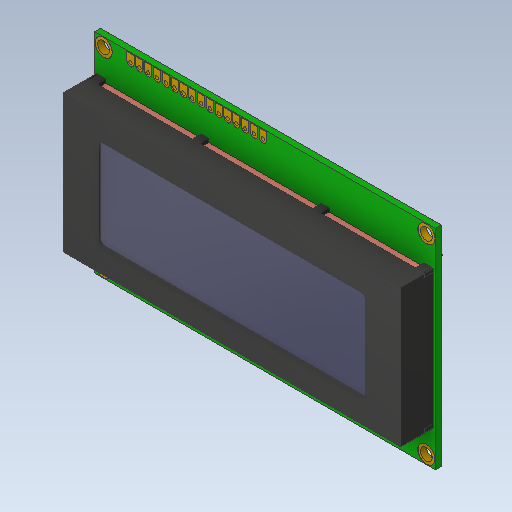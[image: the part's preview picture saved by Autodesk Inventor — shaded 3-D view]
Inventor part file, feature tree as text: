
AUTODESK INVENTOR PART (.ipt)
format: ipt  version: 2020 (Build 240168000, 168)  size: 613,888 bytes
history: native  units: in
note: dims shown in document units (in); Inventor stores cm internally (conversion verified against a paired STEP export)
features: sketch x10, extrude x8, projected_geometry x6, mirror x3, hole x2, fillet x2
ambient origin geometry x8: Origin, YZ Plane, XZ Plane, XY Plane, X Axis, Y Axis, Z Axis, Center Point
bodies: Solid1 (feature_tree)
feature tree (31):
  extrude  "Extrusion1"  Depth=2.371in
  extrude  "Extrusion2"  Depth=0.066in
  mirror  "Mirror1"
  hole  "Hole1"  [1 undecoded]
  extrude  "Extrusion3"  Depth=0.082in
  mirror  "Mirror2"
  hole  "Hole2"  [1 undecoded]
  extrude  "Extrusion4"  Depth=0.1in
  extrude  "Extrusion5"  Depth=3.822in
  extrude  "Extrusion6"  Depth=0.372in TaperAngle=0.0deg
  mirror  "Mirror3"
  extrude  "Extrusion7"  Depth=3.03in
  extrude  "Extrusion8"  Depth=1.021in
  fillet  "Fillet1"  Radius=0.05in
  fillet  "Fillet2"  Radius=0.02in
  sketch  "Sketch1"  dims[d0=3.862in d1=2.371in]
  sketch  "Sketch2"  dims[d2=0.066in d3=0.0in d4=3.66in]
  sketch  "Sketch3"  dims[d5=2.165in d6=0.196in]
  projected_geometry  "Projected Loop1"
  projected_geometry  "Projected Loop2"
  projected_geometry  "Projected Loop3"
  projected_geometry  "Projected Loop4"
  sketch  "Sketch4"  dims[d7=0.001in d8=0.0in]
  sketch  "Sketch5"  dims[d9=0.135in d10=0.75in d11=0.375in d12=0.25in d13=0.5635in d14=1.0in d15=0.8108in d16=0.082in]
  projected_geometry  "Projected Loop5"
  sketch  "Sketch6"  dims[d17=0.089in d18=0.365in]
  sketch  "Sketch7"  dims[d19=0.01in d20=6.2992in d22=0.1in d23=0.3937in d25=1.0in]
  sketch  "Sketch8"  dims[d27=0.001in d28=0.0in]
  projected_geometry  "Projected Loop6"
  sketch  "Sketch9"  dims[d29=0.04in d30=0.75in d31=0.375in d32=0.25in d33=0.5635in d34=1.0in d35=0.8108in d36=3.822in]
  sketch  "Sketch10"  dims[d37=1.567in d38=0.372in d39=0.0in d40=3.03in d41=1.021in d42=0.05in d43=0.02in d44=0.0in d45=1.08in d46=1.08in d50=1.277in d52=0.04in d53=0.0in d54=0.1in d56=0.015in d57=0.005in d58=0.005in d59=0.015in d60=0.2in d61=0.034in d62=0.0825in d63=0.369in d64=0.166in d65=0.088in d66=0.376in d67=0.166in d68=0.7874in d70=1.119in d71=0.3937in d73=1.0in d75=0.1in d76=0.0in d77=0.395in d78=0.862in d79=1.22in d80=1.43in d81=0.885in d82=1.75in d83=0.832in d84=0.914in d85=1.266in d86=0.978in d87=0.816in d88=0.054in d89=0.0in d90=0.19in d91=0.19in d93=0.299in]
note: 2 required parameter values undecoded (feature->parameter linkage not recoverable at this tier; creation-order binding heuristic only, values carry confidence <= 0.55)
